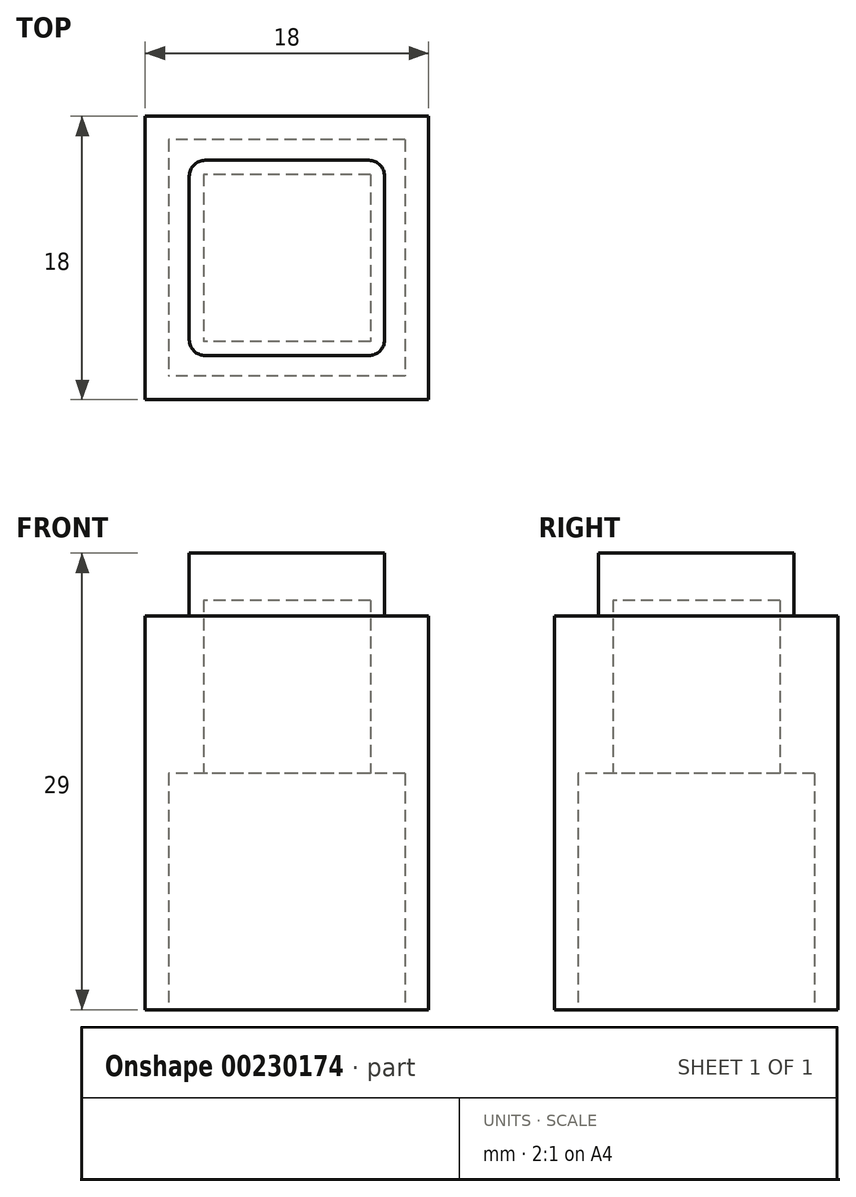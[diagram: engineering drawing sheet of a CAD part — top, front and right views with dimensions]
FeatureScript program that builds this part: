
annotation { "Feature Type Name" : "Feature", "Feature Type Description" : "" }
export const myFeature = defineFeature(function(context is Context, id is Id, definition is map)
    precondition{}
    {
        {
            var Q0;
            Q0=qCreatedBy(makeId("Top.planeOp"),FACE);
            var sketch = newSketch(context, id + "F0", { "sketchPlane" : qUnion([Q0])});
            skLineSegment(sketch, "E0.bottom", {"start": v(-9, 9) * mm, "end": v(9, 9) * mm});
            skLineSegment(sketch, "E0.top", {"start": v(-9, -9) * mm, "end": v(9, -9) * mm});
            skLineSegment(sketch, "E0.left", {"start": v(-9, 9) * mm, "end": v(-9, -9) * mm});
            skLineSegment(sketch, "E0.right", {"start": v(9, 9) * mm, "end": v(9, -9) * mm});
            skPoint(sketch, "E0.middle", {"position": v(0, 0) * mm});
            skSolve(sketch);
        }
        {
            var Q0;
            Q0 = qSketchRegion(id + "F0", true);
            extrude(context, id + "F1", {"entities" : qUnion([Q0]), "depth" : 25 * mm});
        }
        {
            var Q0;
            Q0=makeQuery(id+"F1.opExtrude","CAP_FACE",FACE,{"disambiguationData":[OSD([sQuery(id+"F0.wireOp",EDGE,"E0.bottom"),sQuery(id+"F0.wireOp",EDGE,"E0.top"),sQuery(id+"F0.wireOp",EDGE,"E0.left"),sQuery(id+"F0.wireOp",EDGE,"E0.right")])],"isStart":false});
            var sketch = newSketch(context, id + "F2", { "sketchPlane" : qUnion([Q0])});
            skLineSegment(sketch, "E1.bottom", {"start": v(6.2, -6.2) * mm, "end": v(-6.2, -6.2) * mm});
            skLineSegment(sketch, "E1.top", {"start": v(6.2, 6.2) * mm, "end": v(-6.2, 6.2) * mm});
            skLineSegment(sketch, "E1.left", {"start": v(6.2, -6.2) * mm, "end": v(6.2, 6.2) * mm});
            skLineSegment(sketch, "E1.right", {"start": v(-6.2, -6.2) * mm, "end": v(-6.2, 6.2) * mm});
            skPoint(sketch, "E1.middle", {"position": v(0, 0) * mm});
            skSolve(sketch);
        }
        {
            var Q0;
            Q0=makeQuery(id+"F2.imprint","IMPRINT",FACE,{"disambiguationData":[TD([[makeQuery(id+"F2.imprint","IMPRINT",EDGE,{"derivedFrom":sQuery(id+"F2.wireOp",EDGE,"E1.bottom")}),-1.0]])]});
            extrude(context, id + "F3", {"entities" : qUnion([Q0]), "operationType" : NewBodyOperationType.ADD, "depth" : 4 * mm});
        }
        {
            var Q0;
            Q0=makeQuery(id+"F1.opExtrude","CAP_FACE",FACE,{"disambiguationData":[OSD([sQuery(id+"F0.wireOp",EDGE,"E0.bottom"),sQuery(id+"F0.wireOp",EDGE,"E0.top"),sQuery(id+"F0.wireOp",EDGE,"E0.left"),sQuery(id+"F0.wireOp",EDGE,"E0.right")])],"isStart":true});
            var sketch = newSketch(context, id + "F4", { "sketchPlane" : qUnion([Q0])});
            skLineSegment(sketch, "E2.bottom", {"start": v(7.5, -7.5) * mm, "end": v(-7.5, -7.5) * mm});
            skLineSegment(sketch, "E2.top", {"start": v(7.5, 7.5) * mm, "end": v(-7.5, 7.5) * mm});
            skLineSegment(sketch, "E2.left", {"start": v(7.5, -7.5) * mm, "end": v(7.5, 7.5) * mm});
            skLineSegment(sketch, "E2.right", {"start": v(-7.5, -7.5) * mm, "end": v(-7.5, 7.5) * mm});
            skPoint(sketch, "E2.middle", {"position": v(0, 0) * mm});
            skSolve(sketch);
        }
        {
            var Q0;
            Q0 = qSketchRegion(id + "F4", true);
            extrude(context, id + "F5", {"entities" : qUnion([Q0]), "operationType" : NewBodyOperationType.REMOVE, "oppositeDirection" : true, "depth" : 15 * mm});
        }
        {
            var Q0;
            Q0=makeQuery(id+"F5.boolean.opBoolean","COPY",FACE,{"derivedFrom":makeQuery(id+"F5.opExtrude","CAP_FACE",FACE,{"disambiguationData":[OSD([sQuery(id+"F4.wireOp",EDGE,"E2.bottom"),sQuery(id+"F4.wireOp",EDGE,"E2.top"),sQuery(id+"F4.wireOp",EDGE,"E2.left"),sQuery(id+"F4.wireOp",EDGE,"E2.right")])],"isStart":false})});
            var sketch = newSketch(context, id + "F6", { "sketchPlane" : qUnion([Q0])});
            skLineSegment(sketch, "E3.bottom", {"start": v(5.3, -5.3) * mm, "end": v(-5.3, -5.3) * mm});
            skLineSegment(sketch, "E3.top", {"start": v(5.3, 5.3) * mm, "end": v(-5.3, 5.3) * mm});
            skLineSegment(sketch, "E3.left", {"start": v(5.3, -5.3) * mm, "end": v(5.3, 5.3) * mm});
            skLineSegment(sketch, "E3.right", {"start": v(-5.3, -5.3) * mm, "end": v(-5.3, 5.3) * mm});
            skPoint(sketch, "E3.middle", {"position": v(0, 0) * mm});
            skSolve(sketch);
        }
        {
            var Q0;
            Q0 = qSketchRegion(id + "F6", true);
            extrude(context, id + "F7", {"entities" : qUnion([Q0]), "operationType" : NewBodyOperationType.REMOVE, "oppositeDirection" : true, "depth" : 11 * mm});
        }
        {
            var Q0;
            Q0=makeQuery(id+"F3.opExtrude","SWEPT_EDGE",EDGE,{"disambiguationData":[OSD([sQuery(id+"F2.wireOp",EDGE,"E1.bottom"),sQuery(id+"F2.wireOp",EDGE,"E1.left")])]});
            var Q1;
            Q1=makeQuery(id+"F3.opExtrude","SWEPT_EDGE",EDGE,{"disambiguationData":[OSD([sQuery(id+"F2.wireOp",EDGE,"E1.top"),sQuery(id+"F2.wireOp",EDGE,"E1.left")])]});
            var Q2;
            Q2=makeQuery(id+"F3.opExtrude","SWEPT_EDGE",EDGE,{"disambiguationData":[OSD([sQuery(id+"F2.wireOp",EDGE,"E1.top"),sQuery(id+"F2.wireOp",EDGE,"E1.right")])]});
            var Q3;
            Q3=makeQuery(id+"F3.opExtrude","SWEPT_EDGE",EDGE,{"disambiguationData":[OSD([sQuery(id+"F2.wireOp",EDGE,"E1.bottom"),sQuery(id+"F2.wireOp",EDGE,"E1.right")])]});
            fillet(context, id + "F8", {"entities" : qUnion([Q0, Q1, Q2, Q3]), "radius" : 1 * mm, "tangentPropagation" : true, "allowEdgeOverflow" : false});
        }
    });
